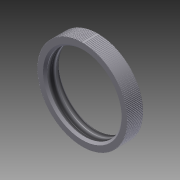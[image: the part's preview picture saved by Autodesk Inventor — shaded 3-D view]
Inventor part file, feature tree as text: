
AUTODESK INVENTOR PART (.ipt)
format: ipt  version: 2011 (Build 150239000, 239)  size: 837,632 bytes
history: native  units: in
note: dims shown in document units (in); Inventor stores cm internally (conversion verified against a paired STEP export)
features: extrude x2, sketch x2, thread x1, pattern_circular x1, chamfer x1
ambient origin geometry x8: Origin, YZ Plane, XZ Plane, XY Plane, X Axis, Y Axis, Z Axis, Center Point
bodies: Solid1 (feature_tree)
feature tree (7):
  extrude  "Extrusion1"  Depth=1.45in
  thread  "Thread1"  [1 undecoded]
  extrude  "Extrusion2"  Depth=0.005in
  pattern_circular  "Circular Pattern1"  [2 undecoded]
  chamfer  "Chamfer1"  Distance=0.25in
  sketch  "Sketch1"  dims[d0=1.2in d1=1.45in d2=0.25in d3=0.0in]
  sketch  "Sketch2"  dims[d4=1.0in d5=0.0in d6=0.005in d7=0.0075in d8=0.25in d9=0.0in d10=78.7402in d11=360.0deg d13=0.0325in d14=0.125in d15=45.0deg]
note: 3 required parameter values undecoded (feature->parameter linkage not recoverable at this tier; creation-order binding heuristic only, values carry confidence <= 0.55)
